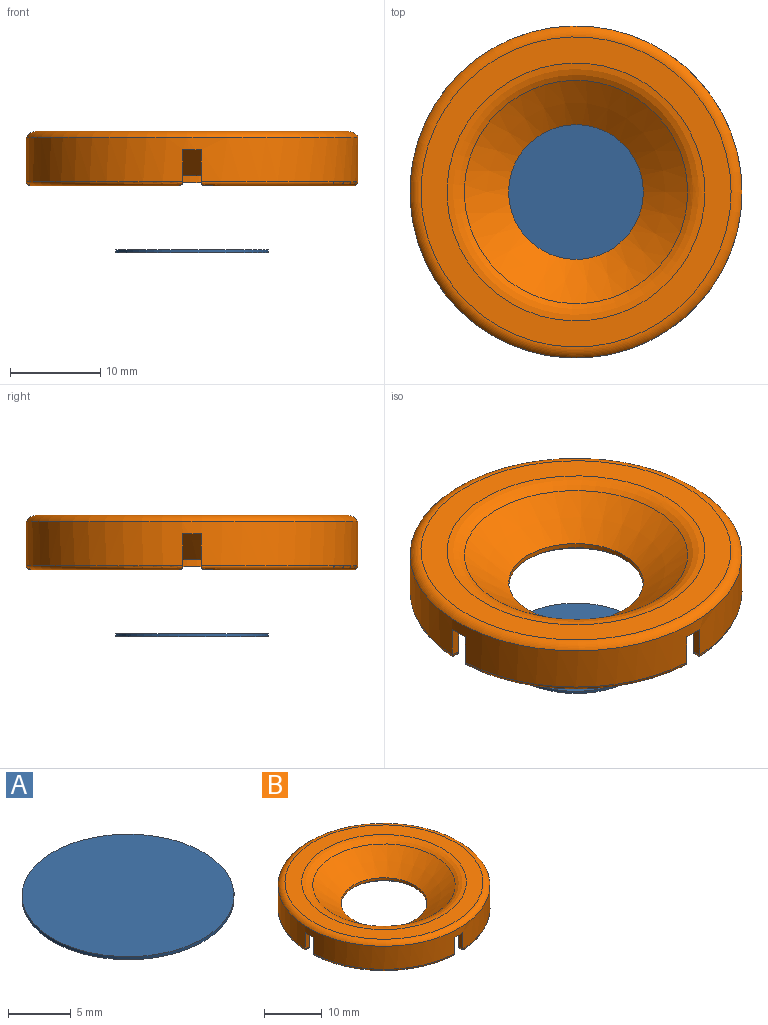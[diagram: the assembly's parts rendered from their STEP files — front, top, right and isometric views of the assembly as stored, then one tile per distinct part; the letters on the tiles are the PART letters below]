
ASSEMBLY  parts=2 mates=2
PART A: 3 faces, bbox 16.9x16.9x0.3 mm
  f0: cylinder r=8.45mm len=16.9mm, axis (0,0,-1), area 15.9mm2, adj f1,f2
  f1: plane 16.9x16.9mm, normal (0,0,1), area 224.3mm2, adj f0
  f2: plane 16.9x16.9mm, normal (0,0,-1), area 224.3mm2, adj f0
PART B: 37 faces, bbox 40.3x40.3x6 mm
  f0: cylinder r=17.38mm len=34.75mm, axis (0,0,1), area 506.9mm2, adj f3,f13,f14,f15,f16,f17,f18,f19
  f1: cylinder r=8.65mm len=17.3mm, axis (0,0,1), area 43.5mm2, adj f2,f12
  f2: cone r=8.65mm half-angle=52.9deg, axis (0,0,1), area 508.2mm2, adj f1,f3
  f3: plane 34.75x34.75mm, normal (0,0,-1), area 308.2mm2, adj f0,f2
  f4: cylinder r=18.38mm len=36.75mm, axis (0,0,1), area 537.7mm2, adj f5,f13,f14,f15,f16,f17,f18,f19
  f5: torus R=17.17mm, axis (0,0,1), area 159.7mm2, adj f4,f6
  f6: plane 34.33x34.33mm, normal (0,0,1), area 285.5mm2, adj f5,f7
  f7: torus R=14.28mm, axis (0,0,1), area 171.8mm2, adj f6,f8
  f8: cone r=7.45mm half-angle=52.9deg, axis (0,0,1), area 383.1mm2, adj f7,f9
  f9: cylinder r=7.45mm len=14.9mm, axis (0,0,1), area 25.4mm2, adj f8,f10
  f10: plane 16.9x16.9mm, normal (0,0,-1), area 50mm2, adj f9,f11
  f11: cylinder r=8.45mm len=16.9mm, axis (0,0,1), area 42.5mm2, adj f10,f12
  f12: plane 17.3x17.3mm, normal (0,0,-1), area 10.7mm2, adj f1,f11
  f13: plane 3.5x1mm, normal (0,1,0), area 3.5mm2, adj f0,f4,f15,f28
  f14: plane 3.5x1mm, normal (0,-1,0), area 3.5mm2, adj f0,f4,f15,f33
  f15: plane 2x1.03mm, normal (0,0,-1), area 2mm2, adj f0,f4,f13,f14
  f16: plane 3.5x1mm, normal (-1,0,0), area 3.5mm2, adj f0,f4,f18,f25
  f17: plane 3.5x1mm, normal (1,0,0), area 3.5mm2, adj f0,f4,f18,f30
  f18: plane 2x1.03mm, normal (0,0,-1), area 2mm2, adj f0,f4,f16,f17
  f19: plane 3.5x1mm, normal (1,0,0), area 3.5mm2, adj f0,f4,f21,f31
  f20: plane 3.5x1mm, normal (-1,0,0), area 3.5mm2, adj f0,f4,f21,f36
  f21: plane 2x1.03mm, normal (0,0,-1), area 2mm2, adj f0,f4,f19,f20
  f22: plane 3.5x1mm, normal (0,1,0), area 3.5mm2, adj f0,f4,f24,f27
  f23: plane 3.5x1mm, normal (0,-1,0), area 3.5mm2, adj f0,f4,f24,f34
  f24: plane 2x1.03mm, normal (0,0,-1), area 2mm2, adj f0,f4,f22,f23
  f25: cylinder r=0.5mm len=1mm, axis (0,-1,0), area 0.5mm2, adj f16,f26
  f26: torus R=17.88mm, axis (0,0,1), area 40.4mm2, adj f0,f4,f25,f27
  f27: cylinder r=0.5mm len=1mm, axis (-1,0,0), area 0.5mm2, adj f22,f26
  f28: cylinder r=0.5mm len=1mm, axis (-1,0,0), area 0.5mm2, adj f13,f29
  f29: torus R=17.88mm, axis (0,0,1), area 40.4mm2, adj f0,f4,f28,f30
  f30: cylinder r=0.5mm len=1mm, axis (0,1,0), area 0.5mm2, adj f17,f29
  f31: cylinder r=0.5mm len=1mm, axis (0,1,0), area 0.5mm2, adj f19,f32
  f32: torus R=17.88mm, axis (0,0,1), area 40.4mm2, adj f0,f4,f31,f33
  f33: cylinder r=0.5mm len=1mm, axis (1,0,0), area 0.5mm2, adj f14,f32
  f34: cylinder r=0.5mm len=1mm, axis (1,0,0), area 0.5mm2, adj f23,f35
  f35: torus R=17.88mm, axis (0,0,1), area 40.4mm2, adj f0,f4,f34,f36
  f36: cylinder r=0.5mm len=1mm, axis (0,-1,0), area 0.5mm2, adj f20,f35
PLACE A t=(-5.63,-0.71,-11.38)mm
PLACE B t=(-5.63,-0.71,-3.98)mm
MATE slider B.f0 <-> A.f0  axis (0,0,-1) through (-5.63,-0.71,-2.84)mm
MATE parallel B.f0 <-> A.f0  axis (0,0,-1) through (-5.63,-0.71,-2.84)mm
